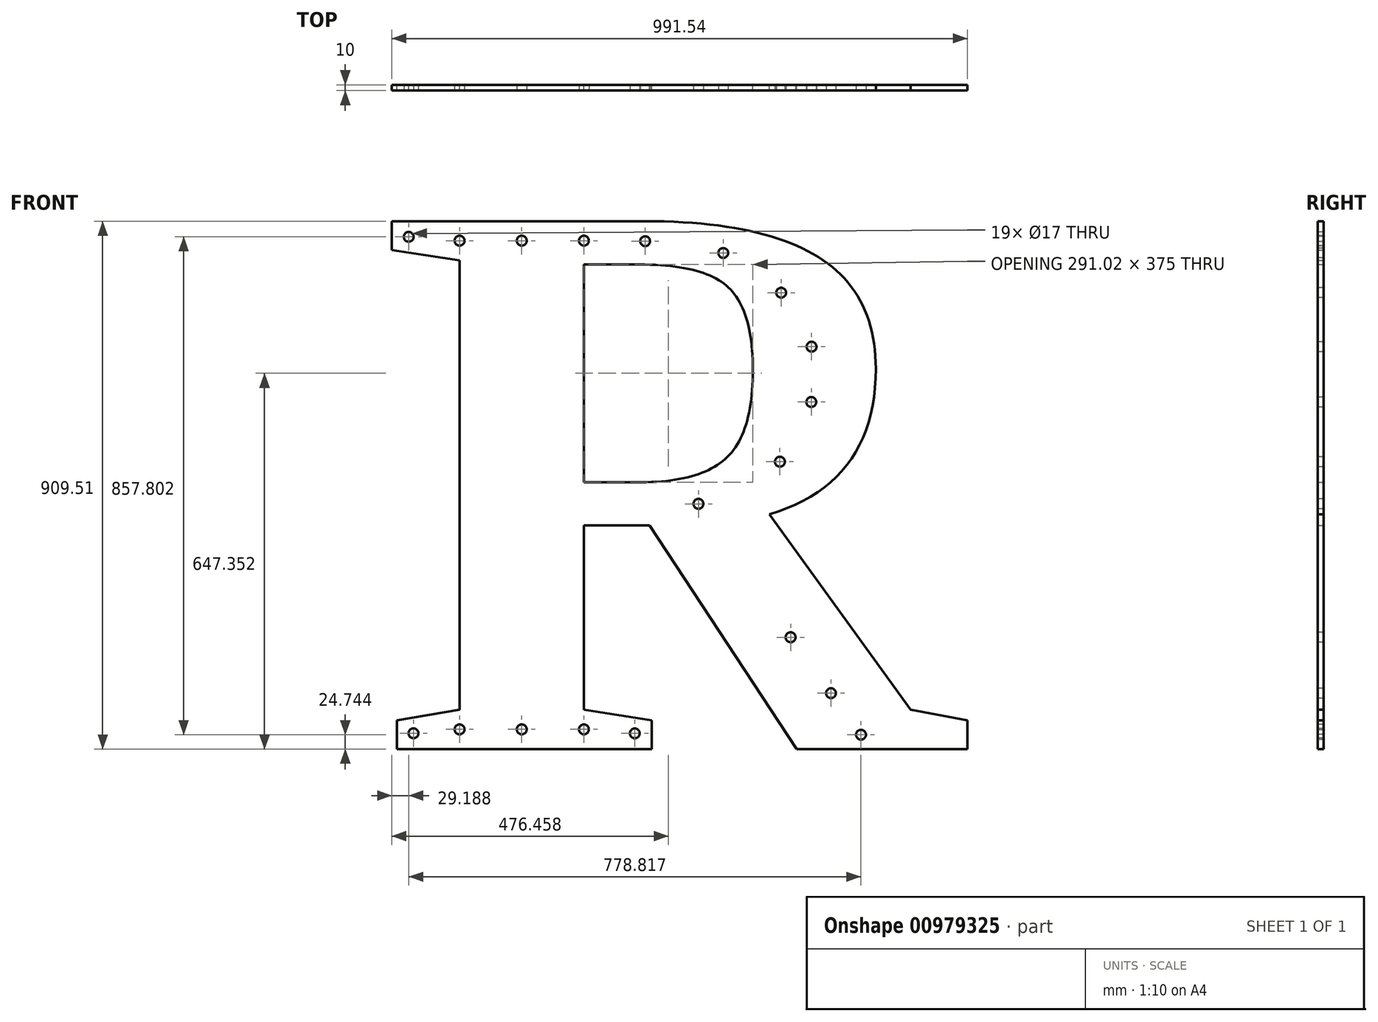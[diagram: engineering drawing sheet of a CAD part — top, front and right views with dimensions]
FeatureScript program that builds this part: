
annotation { "Feature Type Name" : "Feature", "Feature Type Description" : "" }
export const myFeature = defineFeature(function(context is Context, id is Id, definition is map)
    precondition{}
    {
        {
            var Q0;
            Q0=qCreatedBy(makeId("Front.planeOp"),FACE);
            var sketch = newSketch(context, id + "F0", { "sketchPlane" : qUnion([Q0])});
            skText(sketch, "E0", { "text": "R", "fontName": "Tinos-Bold.ttf"});
            const initialGuessF0  = {"E0": [-0.06104, -0.94188, 1, 0, 1]};
            skSetInitialGuess(sketch, initialGuessF0);
            skSolve(sketch);
        }
        {
            var Q0;
            Q0=makeQuery(id+"F0.imprint","IMPRINT",FACE,{"disambiguationData":[TD([[makeQuery(id+"F0.imprint","IMPRINT",EDGE,{"derivedFrom":sQuery(id+"F0.wireOp",EDGE,"E0.sketch_text.stroke-0")}),-1.0]])]});
            extrude(context, id + "F1", {"entities" : qUnion([Q0]), "depth" : 10 * mm, "offsetDistance" : 25 * mm});
        }
        {
            var Q0;
            Q0=makeQuery(id+"F1.opExtrude","SWEPT_FACE",FACE,{"disambiguationData":[OSD([sQuery(id+"F0.wireOp",EDGE,"E0.sketch_text.stroke-8")])]});
            var sketch = newSketch(context, id + "F2", { "sketchPlane" : qUnion([Q0])});
            skLineSegment(sketch, "E1", {"start": v(5, -32.37) * mm, "end": v(50, -32.37) * mm});
            skLineSegment(sketch, "E2", {"start": v(50, -32.37) * mm, "end": v(-50, -32.37) * mm});
            skSolve(sketch);
        }
        {
            var Q0;
            Q0=makeQuery(id+"F1.opExtrude","SWEPT_FACE",FACE,{"disambiguationData":[OSD([sQuery(id+"F0.wireOp",EDGE,"E0.sketch_text.stroke-22")])]});
            var sketch = newSketch(context, id + "F3", { "sketchPlane" : qUnion([Q0])});
            skLineSegment(sketch, "E3", {"start": v(-5, -482.02) * mm, "end": v(40, -482.02) * mm});
            skLineSegment(sketch, "E4", {"start": v(40, -482.02) * mm, "end": v(-60, -482.02) * mm});
            skPoint(sketch, "E4.endSnap0", {"position": v(17.5, -482.02) * mm});
            skSolve(sketch);
        }
        {
            var Q0;
            Q0=makeQuery(id+"F1.opExtrude","CAP_FACE",FACE,{"disambiguationData":[OSD([sQuery(id+"F0.wireOp",EDGE,"E0.sketch_text.stroke-0"),sQuery(id+"F0.wireOp",EDGE,"E0.sketch_text.stroke-1"),sQuery(id+"F0.wireOp",EDGE,"E0.sketch_text.stroke-2"),sQuery(id+"F0.wireOp",EDGE,"E0.sketch_text.stroke-3"),sQuery(id+"F0.wireOp",EDGE,"E0.sketch_text.stroke-4"),sQuery(id+"F0.wireOp",EDGE,"E0.sketch_text.stroke-5"),sQuery(id+"F0.wireOp",EDGE,"E0.sketch_text.stroke-6"),sQuery(id+"F0.wireOp",EDGE,"E0.sketch_text.stroke-7"),sQuery(id+"F0.wireOp",EDGE,"E0.sketch_text.stroke-8"),sQuery(id+"F0.wireOp",EDGE,"E0.sketch_text.stroke-9"),sQuery(id+"F0.wireOp",EDGE,"E0.sketch_text.stroke-10"),sQuery(id+"F0.wireOp",EDGE,"E0.sketch_text.stroke-11"),sQuery(id+"F0.wireOp",EDGE,"E0.sketch_text.stroke-12"),sQuery(id+"F0.wireOp",EDGE,"E0.sketch_text.stroke-13"),sQuery(id+"F0.wireOp",EDGE,"E0.sketch_text.stroke-14"),sQuery(id+"F0.wireOp",EDGE,"E0.sketch_text.stroke-15"),sQuery(id+"F0.wireOp",EDGE,"E0.sketch_text.stroke-16"),sQuery(id+"F0.wireOp",EDGE,"E0.sketch_text.stroke-17"),sQuery(id+"F0.wireOp",EDGE,"E0.sketch_text.stroke-18"),sQuery(id+"F0.wireOp",EDGE,"E0.sketch_text.stroke-19"),sQuery(id+"F0.wireOp",EDGE,"E0.sketch_text.stroke-20"),sQuery(id+"F0.wireOp",EDGE,"E0.sketch_text.stroke-21"),sQuery(id+"F0.wireOp",EDGE,"E0.sketch_text.stroke-22"),sQuery(id+"F0.wireOp",EDGE,"E0.sketch_text.stroke-23"),sQuery(id+"F0.wireOp",EDGE,"E0.sketch_text.stroke-24"),sQuery(id+"F0.wireOp",EDGE,"E0.sketch_text.stroke-25")])],"isStart":false});
            var sketch = newSketch(context, id + "F4", { "sketchPlane" : qUnion([Q0])});
            skPoint(sketch, "E5.endSnap0", {"position": v(-37.4, -57.11) * mm});
            skLineSegment(sketch, "E6", {"start": v(954.15, -917.14) * mm, "end": v(643.58, -917.14) * mm, "construction": true});
            skLineSegment(sketch, "E7", {"start": v(533.03, -749.28) * mm, "end": v(765.83, -749.28) * mm, "construction": true});
            skLineSegment(sketch, "E8", {"start": v(406.19, -556.68) * mm, "end": v(626.79, -556.68) * mm, "construction": true});
            skLineSegment(sketch, "E9", {"start": v(516.49, -556.68) * mm, "end": v(649.43, -749.28) * mm, "construction": true});
            skLineSegment(sketch, "E10", {"start": v(649.43, -749.28) * mm, "end": v(788.48, -941.88) * mm, "construction": true});
            skLineSegment(sketch, "E11", {"start": v(584.57, -288.01) * mm, "end": v(796.16, -286.71) * mm, "construction": true});
            skLineSegment(sketch, "E12", {"start": v(690.37, -287.36) * mm, "end": v(690.37, -502.86) * mm, "construction": true});
            skLineSegment(sketch, "E13", {"start": v(690.37, -287.36) * mm, "end": v(689.15, -89.28) * mm, "construction": true});
            skLineSegment(sketch, "E14", {"start": v(79.36, -99.65) * mm, "end": v(79.36, -32.37) * mm, "construction": true});
            skLineSegment(sketch, "E15", {"start": v(79.36, -66) * mm, "end": v(293.56, -66) * mm, "construction": true});
            skLineSegment(sketch, "E16", {"start": v(79.36, -873.95) * mm, "end": v(79.36, -941.88) * mm, "construction": true});
            skLineSegment(sketch, "E17", {"start": v(79.36, -907.91) * mm, "end": v(-28.5, -917.14) * mm, "construction": true});
            skLineSegment(sketch, "E18", {"start": v(293.56, -873.95) * mm, "end": v(293.56, -941.88) * mm, "construction": true});
            skLineSegment(sketch, "E19", {"start": v(293.56, -907.91) * mm, "end": v(410.3, -917.14) * mm, "construction": true});
            skLineSegment(sketch, "E20", {"start": v(79.36, -907.91) * mm, "end": v(293.56, -907.91) * mm, "construction": true});
            skLineSegment(sketch, "E21", {"start": v(293.56, -107.02) * mm, "end": v(293.56, -32.37) * mm, "construction": true});
            skLineSegment(sketch, "E22", {"start": v(79.36, -66) * mm, "end": v(-37.4, -57.11) * mm, "construction": true});
            skLineSegment(sketch, "E23", {"start": v(293.56, -482.02) * mm, "end": v(293.56, -556.68) * mm});
            skLineSegment(sketch, "E24", {"start": v(293.56, -519.35) * mm, "end": v(79.36, -519.35) * mm, "construction": true});
            skLineSegment(sketch, "E25", {"start": v(293.56, -519.35) * mm, "end": v(660.56, -519.35) * mm, "construction": true});
            skLineSegment(sketch, "E26", {"start": v(584.57, -288.01) * mm, "end": v(584.57, -50.36) * mm, "construction": true});
            skLineSegment(sketch, "E27", {"start": v(584.57, -50.36) * mm, "end": v(584.57, -519.35) * mm, "construction": true});
            skLineSegment(sketch, "E28", {"start": v(186.46, -66) * mm, "end": v(186.46, -907.91) * mm, "construction": true});
            skPoint(sketch, "E29.2.internal.snap0", {"position": v(293.56, -69.7) * mm});
            skFitSpline(sketch, "E29", {"points": [v(293.56, -66) * mm, v(347.38, -66) * mm, v(445.33, -69.7) * mm, v(533.44, -87.18) * mm, v(584.57, -115.36) * mm, v(633.18, -155.61) * mm, v(669.41, -206.16) * mm, v(685.52, -248.65) * mm, v(690.37, -287.36) * mm, v(685.07, -343.92) * mm, v(664.94, -399.82) * mm, v(630.95, -446.79) * mm, v(576.83, -494.65) * mm, v(525.4, -519.35) * mm], "startDerivative": vector(689.57, 2.24) * mm, "endDerivative": vector(-695.48, -274.76) * mm, "construction": true});
            skCircle(sketch, "E30", {"center": v(79.36, -907.91) * mm, "radius": 8.5 * mm});
            skCircle(sketch, "E31", {"center": v(186.46, -907.91) * mm, "radius": 8.5 * mm});
            skCircle(sketch, "E32", {"center": v(293.56, -907.91) * mm, "radius": 8.5 * mm});
            skCircle(sketch, "E33", {"center": v(79.36, -66) * mm, "radius": 8.5 * mm});
            skCircle(sketch, "E34", {"center": v(186.46, -66) * mm, "radius": 8.5 * mm});
            skCircle(sketch, "E35", {"center": v(293.56, -66) * mm, "radius": 8.5 * mm});
            skLineSegment(sketch, "E36", {"start": v(20.99, -61.56) * mm, "end": v(-37.4, -57.11) * mm});
            skCircle(sketch, "E37", {"center": v(-8.2, -59.33) * mm, "radius": 8.5 * mm});
            skLineSegment(sketch, "E38", {"start": v(-28.5, -917.14) * mm, "end": v(25.44, -912.52) * mm});
            skCircle(sketch, "E39", {"center": v(0, -914.7) * mm, "radius": 8.5 * mm});
            skLineSegment(sketch, "E40", {"start": v(410.3, -917.14) * mm, "end": v(351.93, -912.52) * mm});
            skCircle(sketch, "E41", {"center": v(381.12, -914.83) * mm, "radius": 8.5 * mm});
            skLineSegment(sketch, "E42", {"start": v(788.48, -941.88) * mm, "end": v(770.62, -917.14) * mm});
            skCircle(sketch, "E43", {"center": v(770.62, -917.14) * mm, "radius": 8.5 * mm});
            skLineSegment(sketch, "E44", {"start": v(770.62, -917.14) * mm, "end": v(954.15, -917.14) * mm});
            skCircle(sketch, "E45", {"center": v(862.38, -917.14) * mm, "radius": 8.5 * mm});
            skCircle(sketch, "E46", {"center": v(649.43, -749.28) * mm, "radius": 8.5 * mm});
            skLineSegment(sketch, "E47", {"start": v(649.43, -749.28) * mm, "end": v(770.62, -917.14) * mm});
            skCircle(sketch, "E48", {"center": v(718.95, -845.58) * mm, "radius": 8.5 * mm});
            skLineSegment(sketch, "E49", {"start": v(516.49, -556.68) * mm, "end": v(649.43, -749.28) * mm});
            skLineSegment(sketch, "E50", {"start": v(186.46, -519.35) * mm, "end": v(186.46, -907.91) * mm});
            skLineSegment(sketch, "E51", {"start": v(186.46, -907.91) * mm, "end": v(186.46, -713.63) * mm});
            skLineSegment(sketch, "E52", {"start": v(186.46, -713.63) * mm, "end": v(186.46, -810.77) * mm});
            skLineSegment(sketch, "E53", {"start": v(186.46, -713.63) * mm, "end": v(186.46, -519.35) * mm});
            skCircle(sketch, "E54", {"center": v(186.46, -519.35) * mm, "radius": 8.5 * mm});
            skCircle(sketch, "E55", {"center": v(186.46, -616.5) * mm, "radius": 8.5 * mm});
            skCircle(sketch, "E56", {"center": v(186.46, -713.63) * mm, "radius": 8.5 * mm});
            skCircle(sketch, "E57", {"center": v(186.46, -810.77) * mm, "radius": 8.5 * mm});
            skLineSegment(sketch, "E58", {"start": v(186.46, -66) * mm, "end": v(186.46, -519.35) * mm});
            skLineSegment(sketch, "E59", {"start": v(186.46, -292.68) * mm, "end": v(186.46, -66) * mm});
            skLineSegment(sketch, "E60", {"start": v(186.46, -292.68) * mm, "end": v(186.46, -519.35) * mm});
            skCircle(sketch, "E61", {"center": v(186.46, -179.34) * mm, "radius": 8.5 * mm});
            skCircle(sketch, "E62", {"center": v(186.46, -292.68) * mm, "radius": 8.5 * mm});
            skCircle(sketch, "E63", {"center": v(186.46, -406.01) * mm, "radius": 8.5 * mm});
            skLineSegment(sketch, "E64", {"start": v(293.56, -519.35) * mm, "end": v(525.4, -519.35) * mm});
            skCircle(sketch, "E65", {"center": v(630.95, -446.79) * mm, "radius": 8.5 * mm});
            skCircle(sketch, "E66", {"center": v(685.07, -343.92) * mm, "radius": 8.5 * mm});
            skCircle(sketch, "E67", {"center": v(685.52, -248.65) * mm, "radius": 8.5 * mm});
            skCircle(sketch, "E68", {"center": v(633.18, -155.61) * mm, "radius": 8.5 * mm});
            skCircle(sketch, "E69", {"center": v(533.44, -87.18) * mm, "radius": 8.5 * mm});
            skCircle(sketch, "E70", {"center": v(398.92, -66.9) * mm, "radius": 8.5 * mm});
            skLineSegment(sketch, "E71", {"start": v(516.49, -556.68) * mm, "end": v(490.72, -519.35) * mm});
            skCircle(sketch, "E72", {"center": v(490.72, -519.35) * mm, "radius": 8.5 * mm});
            skCircle(sketch, "E73", {"center": v(353, -519.35) * mm, "radius": 8.5 * mm});
            skCircle(sketch, "E74", {"center": v(576.07, -643) * mm, "radius": 8.5 * mm});
            skSolve(sketch);
        }
        {
            var Q0;
            {var subQ0=sQuery(id+"F4.wireOp",EDGE,"E37");var subQ1=sQuery(id+"F4.wireOp",EDGE,"E36");var subQ2=makeQuery(id+"F4.imprint","INTERSECT",VERTEX,{"disambiguationData":[OD(0.0)],"derivedFrom":[subQ1,subQ0]});Q0=makeQuery(id+"F4.imprint","IMPRINT",FACE,{"disambiguationData":[TD([[makeQuery(id+"F4.imprint","IMPRINT",EDGE,{"disambiguationData":[TD([[subQ2,1.0]])],"derivedFrom":subQ1}),-1.0]])]});}
            var Q1;
            {var subQ0=sQuery(id+"F4.wireOp",EDGE,"E37");var subQ1=sQuery(id+"F4.wireOp",EDGE,"E36");var subQ2=makeQuery(id+"F4.imprint","INTERSECT",VERTEX,{"disambiguationData":[OD(0.0)],"derivedFrom":[subQ1,subQ0]});Q1=makeQuery(id+"F4.imprint","IMPRINT",FACE,{"disambiguationData":[TD([[makeQuery(id+"F4.imprint","IMPRINT",EDGE,{"disambiguationData":[TD([[subQ2,1.0]])],"derivedFrom":subQ1}),1.0]])]});}
            var Q2;
            {var subQ0=sQuery(id+"F4.wireOp",EDGE,"E61");var subQ1=sQuery(id+"F4.wireOp",EDGE,"E59");var subQ2=makeQuery(id+"F4.imprint","INTERSECT",VERTEX,{"disambiguationData":[OD(0.0)],"derivedFrom":[subQ1,subQ0]});Q2=makeQuery(id+"F4.imprint","IMPRINT",FACE,{"disambiguationData":[TD([[makeQuery(id+"F4.imprint","IMPRINT",EDGE,{"disambiguationData":[TD([[subQ2,-1.0]])],"derivedFrom":subQ1}),-1.0]])]});}
            var Q3;
            {var subQ0=sQuery(id+"F4.wireOp",EDGE,"E61");var subQ1=sQuery(id+"F4.wireOp",EDGE,"E59");var subQ2=makeQuery(id+"F4.imprint","INTERSECT",VERTEX,{"disambiguationData":[OD(0.0)],"derivedFrom":[subQ1,subQ0]});Q3=makeQuery(id+"F4.imprint","IMPRINT",FACE,{"disambiguationData":[TD([[makeQuery(id+"F4.imprint","IMPRINT",EDGE,{"disambiguationData":[TD([[subQ2,-1.0]])],"derivedFrom":subQ1}),1.0]])]});}
            var Q4;
            Q4=makeQuery(id+"F4.imprint","IMPRINT",FACE,{"disambiguationData":[TD([[makeQuery(id+"F4.imprint","IMPRINT",EDGE,{"derivedFrom":sQuery(id+"F4.wireOp",EDGE,"E33")}),1.0]])]});
            var Q5;
            Q5=makeQuery(id+"F4.imprint","IMPRINT",FACE,{"disambiguationData":[TD([[makeQuery(id+"F4.imprint","IMPRINT",EDGE,{"derivedFrom":sQuery(id+"F4.wireOp",EDGE,"E34")}),1.0]])]});
            var Q6;
            {var subQ0=sQuery(id+"F4.wireOp",EDGE,"E60");var subQ1=sQuery(id+"F4.wireOp",EDGE,"E59");var subQ2=makeQuery(id+"F4.imprint","INTERSECT",VERTEX,{"derivedFrom":[subQ1,subQ0]});Q6=makeQuery(id+"F4.imprint","IMPRINT",FACE,{"disambiguationData":[TD([[makeQuery(id+"F4.imprint","IMPRINT",EDGE,{"disambiguationData":[TD([[subQ2,-1.0]])],"derivedFrom":subQ1}),-1.0]])]});}
            var Q7;
            {var subQ0=sQuery(id+"F4.wireOp",EDGE,"E60");var subQ1=sQuery(id+"F4.wireOp",EDGE,"E59");var subQ2=makeQuery(id+"F4.imprint","INTERSECT",VERTEX,{"derivedFrom":[subQ1,subQ0]});Q7=makeQuery(id+"F4.imprint","IMPRINT",FACE,{"disambiguationData":[TD([[makeQuery(id+"F4.imprint","IMPRINT",EDGE,{"disambiguationData":[TD([[subQ2,-1.0]])],"derivedFrom":subQ1}),1.0]])]});}
            var Q8;
            {var subQ0=sQuery(id+"F4.wireOp",EDGE,"E63");var subQ1=sQuery(id+"F4.wireOp",EDGE,"E60");var subQ2=makeQuery(id+"F4.imprint","INTERSECT",VERTEX,{"disambiguationData":[OD(0.0)],"derivedFrom":[subQ1,subQ0]});Q8=makeQuery(id+"F4.imprint","IMPRINT",FACE,{"disambiguationData":[TD([[makeQuery(id+"F4.imprint","IMPRINT",EDGE,{"disambiguationData":[TD([[subQ2,1.0]])],"derivedFrom":subQ1}),1.0]])]});}
            var Q9;
            {var subQ0=sQuery(id+"F4.wireOp",EDGE,"E63");var subQ1=sQuery(id+"F4.wireOp",EDGE,"E60");var subQ2=makeQuery(id+"F4.imprint","INTERSECT",VERTEX,{"disambiguationData":[OD(0.0)],"derivedFrom":[subQ1,subQ0]});Q9=makeQuery(id+"F4.imprint","IMPRINT",FACE,{"disambiguationData":[TD([[makeQuery(id+"F4.imprint","IMPRINT",EDGE,{"disambiguationData":[TD([[subQ2,1.0]])],"derivedFrom":subQ1}),-1.0]])]});}
            var Q10;
            {var subQ0=sQuery(id+"F4.wireOp",EDGE,"E60");var subQ1=sQuery(id+"F4.wireOp",EDGE,"E53");var subQ2=makeQuery(id+"F4.imprint","INTERSECT",VERTEX,{"derivedFrom":[subQ1,subQ0]});Q10=makeQuery(id+"F4.imprint","IMPRINT",FACE,{"disambiguationData":[TD([[makeQuery(id+"F4.imprint","IMPRINT",EDGE,{"disambiguationData":[TD([[subQ2,1.0]])],"derivedFrom":subQ1}),-1.0]])]});}
            var Q11;
            {var subQ0=sQuery(id+"F4.wireOp",EDGE,"E60");var subQ1=sQuery(id+"F4.wireOp",EDGE,"E53");var subQ2=makeQuery(id+"F4.imprint","INTERSECT",VERTEX,{"derivedFrom":[subQ1,subQ0]});Q11=makeQuery(id+"F4.imprint","IMPRINT",FACE,{"disambiguationData":[TD([[makeQuery(id+"F4.imprint","IMPRINT",EDGE,{"disambiguationData":[TD([[subQ2,1.0]])],"derivedFrom":subQ1}),1.0]])]});}
            var Q12;
            {var subQ0=sQuery(id+"F4.wireOp",EDGE,"E23");var subQ1=makeQuery(id+"F4.imprint","INTERSECT",VERTEX,{"derivedFrom":[subQ0,sQuery(id+"F4.wireOp",EDGE,"E64")]});Q12=makeQuery(id+"F4.imprint","IMPRINT",FACE,{"disambiguationData":[TD([[makeQuery(id+"F4.imprint","IMPRINT",EDGE,{"disambiguationData":[TD([[subQ1,1.0]])],"derivedFrom":subQ0}),-1.0]])]});}
            var Q13;
            {var subQ0=sQuery(id+"F4.wireOp",EDGE,"E64");var subQ1=sQuery(id+"F4.wireOp",EDGE,"E23");var subQ2=makeQuery(id+"F4.imprint","INTERSECT",VERTEX,{"derivedFrom":[subQ1,subQ0]});Q13=makeQuery(id+"F4.imprint","IMPRINT",FACE,{"disambiguationData":[TD([[makeQuery(id+"F4.imprint","IMPRINT",EDGE,{"disambiguationData":[TD([[subQ2,1.0]])],"derivedFrom":subQ1}),1.0]])]});}
            var Q14;
            {var subQ0=sQuery(id+"F4.wireOp",EDGE,"E55");var subQ1=sQuery(id+"F4.wireOp",EDGE,"E53");var subQ2=makeQuery(id+"F4.imprint","INTERSECT",VERTEX,{"disambiguationData":[OD(0.0)],"derivedFrom":[subQ1,subQ0]});Q14=makeQuery(id+"F4.imprint","IMPRINT",FACE,{"disambiguationData":[TD([[makeQuery(id+"F4.imprint","IMPRINT",EDGE,{"disambiguationData":[TD([[subQ2,-1.0]])],"derivedFrom":subQ1}),-1.0]])]});}
            var Q15;
            {var subQ0=sQuery(id+"F4.wireOp",EDGE,"E55");var subQ1=sQuery(id+"F4.wireOp",EDGE,"E53");var subQ2=makeQuery(id+"F4.imprint","INTERSECT",VERTEX,{"disambiguationData":[OD(0.0)],"derivedFrom":[subQ1,subQ0]});Q15=makeQuery(id+"F4.imprint","IMPRINT",FACE,{"disambiguationData":[TD([[makeQuery(id+"F4.imprint","IMPRINT",EDGE,{"disambiguationData":[TD([[subQ2,-1.0]])],"derivedFrom":subQ1}),1.0]])]});}
            var Q16;
            {var subQ0=sQuery(id+"F4.wireOp",EDGE,"E53");var subQ1=sQuery(id+"F4.wireOp",EDGE,"E52");var subQ2=makeQuery(id+"F4.imprint","INTERSECT",VERTEX,{"derivedFrom":[subQ1,subQ0]});Q16=makeQuery(id+"F4.imprint","IMPRINT",FACE,{"disambiguationData":[TD([[makeQuery(id+"F4.imprint","IMPRINT",EDGE,{"disambiguationData":[TD([[subQ2,-1.0]])],"derivedFrom":subQ1}),1.0]])]});}
            var Q17;
            {var subQ0=sQuery(id+"F4.wireOp",EDGE,"E53");var subQ1=sQuery(id+"F4.wireOp",EDGE,"E52");var subQ2=makeQuery(id+"F4.imprint","INTERSECT",VERTEX,{"derivedFrom":[subQ1,subQ0]});Q17=makeQuery(id+"F4.imprint","IMPRINT",FACE,{"disambiguationData":[TD([[makeQuery(id+"F4.imprint","IMPRINT",EDGE,{"disambiguationData":[TD([[subQ2,-1.0]])],"derivedFrom":subQ1}),-1.0]])]});}
            var Q18;
            {var subQ0=sQuery(id+"F4.wireOp",EDGE,"E52");var subQ1=sQuery(id+"F4.wireOp",EDGE,"E51");var subQ2=makeQuery(id+"F4.imprint","INTERSECT",VERTEX,{"derivedFrom":[subQ1,subQ0]});Q18=makeQuery(id+"F4.imprint","IMPRINT",FACE,{"disambiguationData":[TD([[makeQuery(id+"F4.imprint","IMPRINT",EDGE,{"disambiguationData":[TD([[subQ2,1.0]])],"derivedFrom":subQ1}),-1.0]])]});}
            var Q19;
            {var subQ0=sQuery(id+"F4.wireOp",EDGE,"E52");var subQ1=sQuery(id+"F4.wireOp",EDGE,"E51");var subQ2=makeQuery(id+"F4.imprint","INTERSECT",VERTEX,{"derivedFrom":[subQ1,subQ0]});Q19=makeQuery(id+"F4.imprint","IMPRINT",FACE,{"disambiguationData":[TD([[makeQuery(id+"F4.imprint","IMPRINT",EDGE,{"disambiguationData":[TD([[subQ2,1.0]])],"derivedFrom":subQ1}),1.0]])]});}
            var Q20;
            Q20=makeQuery(id+"F4.imprint","IMPRINT",FACE,{"disambiguationData":[TD([[makeQuery(id+"F4.imprint","IMPRINT",EDGE,{"derivedFrom":sQuery(id+"F4.wireOp",EDGE,"E31")}),1.0]])]});
            var Q21;
            Q21=makeQuery(id+"F4.imprint","IMPRINT",FACE,{"disambiguationData":[TD([[makeQuery(id+"F4.imprint","IMPRINT",EDGE,{"derivedFrom":sQuery(id+"F4.wireOp",EDGE,"E32")}),1.0]])]});
            var Q22;
            {var subQ0=sQuery(id+"F4.wireOp",EDGE,"E41");var subQ1=sQuery(id+"F4.wireOp",EDGE,"E40");var subQ2=makeQuery(id+"F4.imprint","INTERSECT",VERTEX,{"disambiguationData":[OD(0.0)],"derivedFrom":[subQ1,subQ0]});Q22=makeQuery(id+"F4.imprint","IMPRINT",FACE,{"disambiguationData":[TD([[makeQuery(id+"F4.imprint","IMPRINT",EDGE,{"disambiguationData":[TD([[subQ2,1.0]])],"derivedFrom":subQ1}),1.0]])]});}
            var Q23;
            {var subQ0=sQuery(id+"F4.wireOp",EDGE,"E41");var subQ1=sQuery(id+"F4.wireOp",EDGE,"E40");var subQ2=makeQuery(id+"F4.imprint","INTERSECT",VERTEX,{"disambiguationData":[OD(0.0)],"derivedFrom":[subQ1,subQ0]});Q23=makeQuery(id+"F4.imprint","IMPRINT",FACE,{"disambiguationData":[TD([[makeQuery(id+"F4.imprint","IMPRINT",EDGE,{"disambiguationData":[TD([[subQ2,1.0]])],"derivedFrom":subQ1}),-1.0]])]});}
            var Q24;
            Q24=makeQuery(id+"F4.imprint","IMPRINT",FACE,{"disambiguationData":[TD([[makeQuery(id+"F4.imprint","IMPRINT",EDGE,{"derivedFrom":sQuery(id+"F4.wireOp",EDGE,"E30")}),1.0]])]});
            var Q25;
            {var subQ0=sQuery(id+"F4.wireOp",EDGE,"E39");var subQ1=sQuery(id+"F4.wireOp",EDGE,"E38");var subQ2=makeQuery(id+"F4.imprint","INTERSECT",VERTEX,{"disambiguationData":[OD(0.0)],"derivedFrom":[subQ1,subQ0]});Q25=makeQuery(id+"F4.imprint","IMPRINT",FACE,{"disambiguationData":[TD([[makeQuery(id+"F4.imprint","IMPRINT",EDGE,{"disambiguationData":[TD([[subQ2,-1.0]])],"derivedFrom":subQ1}),1.0]])]});}
            var Q26;
            {var subQ0=sQuery(id+"F4.wireOp",EDGE,"E39");var subQ1=sQuery(id+"F4.wireOp",EDGE,"E38");var subQ2=makeQuery(id+"F4.imprint","INTERSECT",VERTEX,{"disambiguationData":[OD(0.0)],"derivedFrom":[subQ1,subQ0]});Q26=makeQuery(id+"F4.imprint","IMPRINT",FACE,{"disambiguationData":[TD([[makeQuery(id+"F4.imprint","IMPRINT",EDGE,{"disambiguationData":[TD([[subQ2,-1.0]])],"derivedFrom":subQ1}),-1.0]])]});}
            var Q27;
            {var subQ0=sQuery(id+"F4.wireOp",EDGE,"E45");var subQ1=sQuery(id+"F4.wireOp",EDGE,"E44");var subQ2=makeQuery(id+"F4.imprint","INTERSECT",VERTEX,{"disambiguationData":[OD(0.0)],"derivedFrom":[subQ1,subQ0]});Q27=makeQuery(id+"F4.imprint","IMPRINT",FACE,{"disambiguationData":[TD([[makeQuery(id+"F4.imprint","IMPRINT",EDGE,{"disambiguationData":[TD([[subQ2,-1.0]])],"derivedFrom":subQ1}),-1.0]])]});}
            var Q28;
            {var subQ0=sQuery(id+"F4.wireOp",EDGE,"E45");var subQ1=sQuery(id+"F4.wireOp",EDGE,"E44");var subQ2=makeQuery(id+"F4.imprint","INTERSECT",VERTEX,{"disambiguationData":[OD(0.0)],"derivedFrom":[subQ1,subQ0]});Q28=makeQuery(id+"F4.imprint","IMPRINT",FACE,{"disambiguationData":[TD([[makeQuery(id+"F4.imprint","IMPRINT",EDGE,{"disambiguationData":[TD([[subQ2,-1.0]])],"derivedFrom":subQ1}),1.0]])]});}
            var Q29;
            {var subQ0=sQuery(id+"F4.wireOp",EDGE,"E47");var subQ1=sQuery(id+"F4.wireOp",EDGE,"E43");var subQ2=makeQuery(id+"F4.imprint","INTERSECT",VERTEX,{"derivedFrom":[subQ1,subQ0]});Q29=makeQuery(id+"F4.imprint","IMPRINT",FACE,{"disambiguationData":[TD([[makeQuery(id+"F4.imprint","IMPRINT",EDGE,{"disambiguationData":[TD([[subQ2,1.0]])],"derivedFrom":subQ1}),1.0]])]});}
            var Q30;
            {var subQ0=sQuery(id+"F4.wireOp",EDGE,"E47");var subQ3=sQuery(id+"F4.wireOp",EDGE,"E43");var subQ5=makeQuery(id+"F4.imprint","INTERSECT",VERTEX,{"derivedFrom":[subQ3,subQ0]});Q30=makeQuery(id+"F4.imprint","IMPRINT",FACE,{"disambiguationData":[TD([[makeQuery(id+"F4.imprint","IMPRINT",EDGE,{"disambiguationData":[TD([[subQ5,-1.0]])],"derivedFrom":subQ3}),1.0]])]});}
            var Q31;
            {var subQ1=sQuery(id+"F4.wireOp",EDGE,"E42");var subQ3=sQuery(id+"F4.wireOp",EDGE,"E43");var subQ4=makeQuery(id+"F4.imprint","INTERSECT",VERTEX,{"derivedFrom":[subQ1,subQ3]});Q31=makeQuery(id+"F4.imprint","IMPRINT",FACE,{"disambiguationData":[TD([[makeQuery(id+"F4.imprint","IMPRINT",EDGE,{"disambiguationData":[TD([[subQ4,-1.0]])],"derivedFrom":subQ3}),1.0]])]});}
            var Q32;
            {var subQ0=sQuery(id+"F4.wireOp",EDGE,"E48");var subQ1=sQuery(id+"F4.wireOp",EDGE,"E47");var subQ2=makeQuery(id+"F4.imprint","INTERSECT",VERTEX,{"disambiguationData":[OD(0.0)],"derivedFrom":[subQ1,subQ0]});Q32=makeQuery(id+"F4.imprint","IMPRINT",FACE,{"disambiguationData":[TD([[makeQuery(id+"F4.imprint","IMPRINT",EDGE,{"disambiguationData":[TD([[subQ2,-1.0]])],"derivedFrom":subQ1}),1.0]])]});}
            var Q33;
            {var subQ0=sQuery(id+"F4.wireOp",EDGE,"E48");var subQ1=sQuery(id+"F4.wireOp",EDGE,"E47");var subQ2=makeQuery(id+"F4.imprint","INTERSECT",VERTEX,{"disambiguationData":[OD(0.0)],"derivedFrom":[subQ1,subQ0]});Q33=makeQuery(id+"F4.imprint","IMPRINT",FACE,{"disambiguationData":[TD([[makeQuery(id+"F4.imprint","IMPRINT",EDGE,{"disambiguationData":[TD([[subQ2,-1.0]])],"derivedFrom":subQ1}),-1.0]])]});}
            var Q34;
            {var subQ0=sQuery(id+"F4.wireOp",EDGE,"E47");var subQ1=sQuery(id+"F4.wireOp",EDGE,"E46");var subQ2=makeQuery(id+"F4.imprint","INTERSECT",VERTEX,{"derivedFrom":[subQ1,subQ0]});Q34=makeQuery(id+"F4.imprint","IMPRINT",FACE,{"disambiguationData":[TD([[makeQuery(id+"F4.imprint","IMPRINT",EDGE,{"disambiguationData":[TD([[subQ2,1.0]])],"derivedFrom":subQ1}),1.0]])]});}
            var Q35;
            {var subQ0=sQuery(id+"F4.wireOp",EDGE,"E47");var subQ1=sQuery(id+"F4.wireOp",EDGE,"E46");var subQ2=makeQuery(id+"F4.imprint","INTERSECT",VERTEX,{"derivedFrom":[subQ1,subQ0]});Q35=makeQuery(id+"F4.imprint","IMPRINT",FACE,{"disambiguationData":[TD([[makeQuery(id+"F4.imprint","IMPRINT",EDGE,{"disambiguationData":[TD([[subQ2,-1.0]])],"derivedFrom":subQ1}),1.0]])]});}
            var Q36;
            {var subQ0=sQuery(id+"F4.wireOp",EDGE,"7aU0Kaek-DPU5-1L0Z-JC4m-BMOp5fFMClNH");var subQ1=sQuery(id+"F4.wireOp",EDGE,"E64");var subQ2=makeQuery(id+"F4.imprint","INTERSECT",VERTEX,{"disambiguationData":[OD(0.0)],"derivedFrom":[subQ1,subQ0]});Q36=makeQuery(id+"F4.imprint","IMPRINT",FACE,{"disambiguationData":[TD([[makeQuery(id+"F4.imprint","IMPRINT",EDGE,{"disambiguationData":[TD([[subQ2,-1.0]])],"derivedFrom":subQ1}),1.0]])]});}
            var Q37;
            {var subQ0=sQuery(id+"F4.wireOp",EDGE,"7aU0Kaek-DPU5-1L0Z-JC4m-BMOp5fFMClNH");var subQ1=sQuery(id+"F4.wireOp",EDGE,"E64");var subQ2=makeQuery(id+"F4.imprint","INTERSECT",VERTEX,{"disambiguationData":[OD(0.0)],"derivedFrom":[subQ1,subQ0]});Q37=makeQuery(id+"F4.imprint","IMPRINT",FACE,{"disambiguationData":[TD([[makeQuery(id+"F4.imprint","IMPRINT",EDGE,{"disambiguationData":[TD([[subQ2,-1.0]])],"derivedFrom":subQ1}),-1.0]])]});}
            var Q38;
            Q38=makeQuery(id+"F4.imprint","IMPRINT",FACE,{"disambiguationData":[TD([[makeQuery(id+"F4.imprint","IMPRINT",EDGE,{"derivedFrom":sQuery(id+"F4.wireOp",EDGE,"E65")}),1.0]])]});
            var Q39;
            Q39=makeQuery(id+"F4.imprint","IMPRINT",FACE,{"disambiguationData":[TD([[makeQuery(id+"F4.imprint","IMPRINT",EDGE,{"derivedFrom":sQuery(id+"F4.wireOp",EDGE,"E66")}),1.0]])]});
            var Q40;
            Q40=makeQuery(id+"F4.imprint","IMPRINT",FACE,{"disambiguationData":[TD([[makeQuery(id+"F4.imprint","IMPRINT",EDGE,{"derivedFrom":sQuery(id+"F4.wireOp",EDGE,"E67")}),1.0]])]});
            var Q41;
            Q41=makeQuery(id+"F4.imprint","IMPRINT",FACE,{"disambiguationData":[TD([[makeQuery(id+"F4.imprint","IMPRINT",EDGE,{"derivedFrom":sQuery(id+"F4.wireOp",EDGE,"E68")}),1.0]])]});
            var Q42;
            Q42=makeQuery(id+"F4.imprint","IMPRINT",FACE,{"disambiguationData":[TD([[makeQuery(id+"F4.imprint","IMPRINT",EDGE,{"derivedFrom":sQuery(id+"F4.wireOp",EDGE,"E69")}),1.0]])]});
            var Q43;
            Q43=makeQuery(id+"F4.imprint","IMPRINT",FACE,{"disambiguationData":[TD([[makeQuery(id+"F4.imprint","IMPRINT",EDGE,{"derivedFrom":sQuery(id+"F4.wireOp",EDGE,"E70")}),1.0]])]});
            var Q44;
            Q44=makeQuery(id+"F4.imprint","IMPRINT",FACE,{"disambiguationData":[TD([[makeQuery(id+"F4.imprint","IMPRINT",EDGE,{"derivedFrom":sQuery(id+"F4.wireOp",EDGE,"E35")}),1.0]])]});
            var Q45;
            Q45=makeQuery(id+"F4.imprint","IMPRINT",FACE,{"disambiguationData":[TD([[makeQuery(id+"F4.imprint","IMPRINT",EDGE,{"derivedFrom":sQuery(id+"F4.wireOp",EDGE,"aR7mkGp8-7cHy-K9Ln-gFuW-66wq1VA9sPGa")}),1.0]])]});
            var Q46;
            {var subQ0=sQuery(id+"F4.wireOp",EDGE,"ISxmnO5B-mtkN-VL2n-f4vy-AKWv3bSall8z");var subQ1=sQuery(id+"F4.wireOp",EDGE,"E71");var subQ2=makeQuery(id+"F4.imprint","INTERSECT",VERTEX,{"disambiguationData":[OD(0.0)],"derivedFrom":[subQ1,subQ0]});Q46=makeQuery(id+"F4.imprint","IMPRINT",FACE,{"disambiguationData":[TD([[makeQuery(id+"F4.imprint","IMPRINT",EDGE,{"disambiguationData":[TD([[subQ2,-1.0]])],"derivedFrom":subQ1}),1.0]])]});}
            var Q47;
            {var subQ0=sQuery(id+"F4.wireOp",EDGE,"ISxmnO5B-mtkN-VL2n-f4vy-AKWv3bSall8z");var subQ1=sQuery(id+"F4.wireOp",EDGE,"E71");var subQ2=makeQuery(id+"F4.imprint","INTERSECT",VERTEX,{"disambiguationData":[OD(0.0)],"derivedFrom":[subQ1,subQ0]});Q47=makeQuery(id+"F4.imprint","IMPRINT",FACE,{"disambiguationData":[TD([[makeQuery(id+"F4.imprint","IMPRINT",EDGE,{"disambiguationData":[TD([[subQ2,-1.0]])],"derivedFrom":subQ1}),-1.0]])]});}
            var Q48;
            {var subQ0=sQuery(id+"F4.wireOp",EDGE,"E64");var subQ1=makeQuery(id+"F4.imprint","INTERSECT",VERTEX,{"derivedFrom":[subQ0,sQuery(id+"F4.wireOp",EDGE,"E71")]});Q48=makeQuery(id+"F4.imprint","IMPRINT",FACE,{"disambiguationData":[TD([[makeQuery(id+"F4.imprint","IMPRINT",EDGE,{"disambiguationData":[TD([[subQ1,1.0]])],"derivedFrom":subQ0}),1.0]])]});}
            var Q49;
            {var subQ0=sQuery(id+"F4.wireOp",EDGE,"E73");var subQ1=sQuery(id+"F4.wireOp",EDGE,"E64");var subQ2=makeQuery(id+"F4.imprint","INTERSECT",VERTEX,{"disambiguationData":[OD(0.0)],"derivedFrom":[subQ1,subQ0]});Q49=makeQuery(id+"F4.imprint","IMPRINT",FACE,{"disambiguationData":[TD([[makeQuery(id+"F4.imprint","IMPRINT",EDGE,{"disambiguationData":[TD([[subQ2,-1.0]])],"derivedFrom":subQ1}),-1.0]])]});}
            var Q50;
            {var subQ0=sQuery(id+"F4.wireOp",EDGE,"E73");var subQ1=sQuery(id+"F4.wireOp",EDGE,"E64");var subQ2=makeQuery(id+"F4.imprint","INTERSECT",VERTEX,{"disambiguationData":[OD(0.0)],"derivedFrom":[subQ1,subQ0]});Q50=makeQuery(id+"F4.imprint","IMPRINT",FACE,{"disambiguationData":[TD([[makeQuery(id+"F4.imprint","IMPRINT",EDGE,{"disambiguationData":[TD([[subQ2,-1.0]])],"derivedFrom":subQ1}),1.0]])]});}
            var Q51;
            {var subQ0=sQuery(id+"F4.wireOp",EDGE,"E74");var subQ1=sQuery(id+"F4.wireOp",EDGE,"E49");var subQ2=makeQuery(id+"F4.imprint","INTERSECT",VERTEX,{"disambiguationData":[OD(0.0)],"derivedFrom":[subQ1,subQ0]});Q51=makeQuery(id+"F4.imprint","IMPRINT",FACE,{"disambiguationData":[TD([[makeQuery(id+"F4.imprint","IMPRINT",EDGE,{"disambiguationData":[TD([[subQ2,-1.0]])],"derivedFrom":subQ1}),1.0]])]});}
            var Q52;
            {var subQ0=sQuery(id+"F4.wireOp",EDGE,"E74");var subQ1=sQuery(id+"F4.wireOp",EDGE,"E49");var subQ2=makeQuery(id+"F4.imprint","INTERSECT",VERTEX,{"disambiguationData":[OD(0.0)],"derivedFrom":[subQ1,subQ0]});Q52=makeQuery(id+"F4.imprint","IMPRINT",FACE,{"disambiguationData":[TD([[makeQuery(id+"F4.imprint","IMPRINT",EDGE,{"disambiguationData":[TD([[subQ2,-1.0]])],"derivedFrom":subQ1}),-1.0]])]});}
            extrude(context, id + "F5", {"entities" : qUnion([Q0, Q1, Q2, Q3, Q4, Q5, Q6, Q7, Q8, Q9, Q10, Q11, Q12, Q13, Q14, Q15, Q16, Q17, Q18, Q19, Q20, Q21, Q22, Q23, Q24, Q25, Q26, Q27, Q28, Q29, Q30, Q31, Q32, Q33, Q34, Q35, Q36, Q37, Q38, Q39, Q40, Q41, Q42, Q43, Q44, Q45, Q46, Q47, Q48, Q49, Q50, Q51, Q52]), "operationType" : NewBodyOperationType.REMOVE, "endBound" : BoundingType.SYMMETRIC, "oppositeDirection" : true, "depth" : 25 * mm, "offsetDistance" : 25 * mm});
        }
    });
